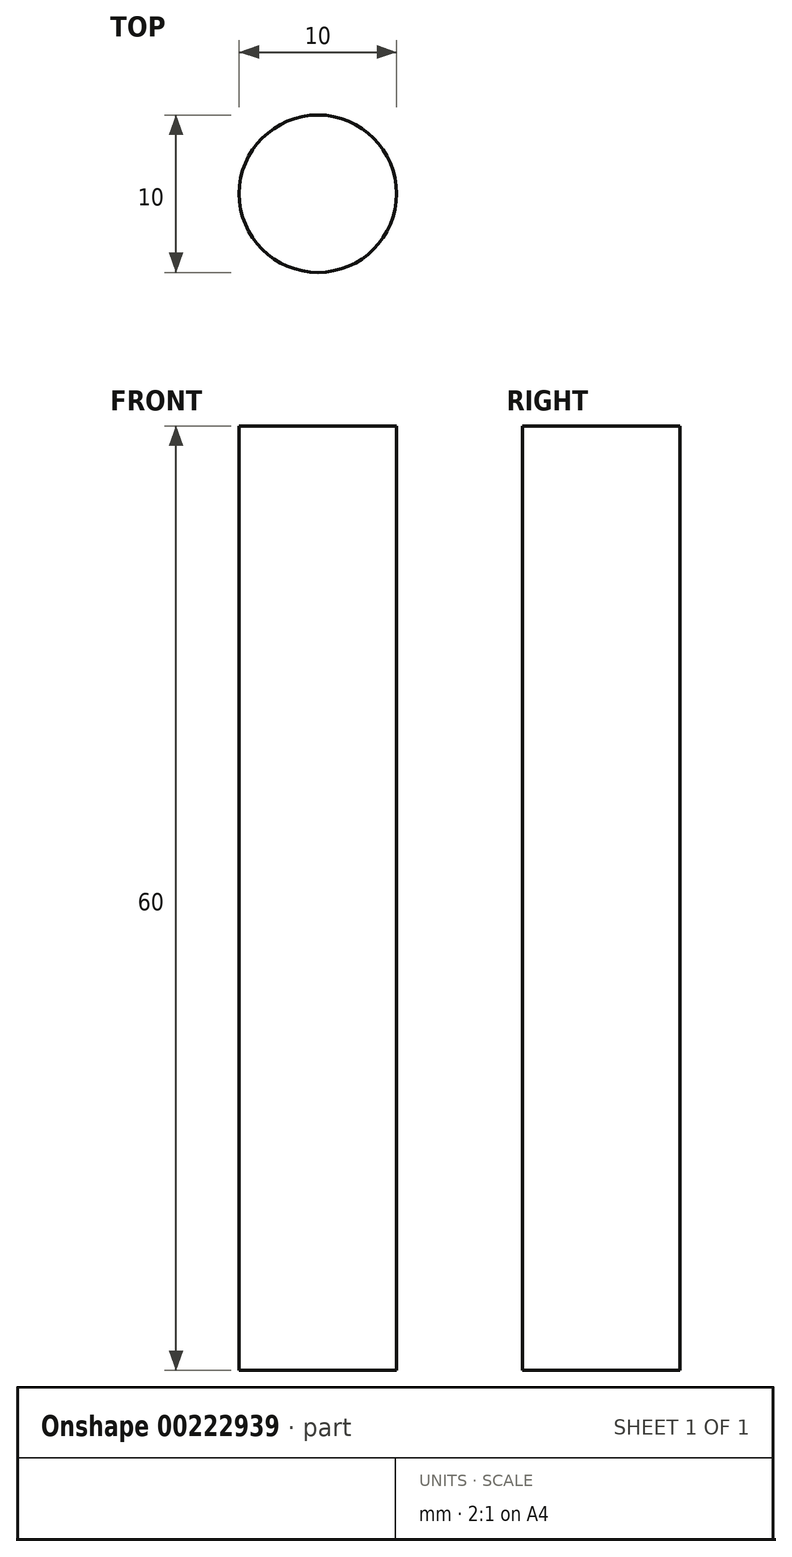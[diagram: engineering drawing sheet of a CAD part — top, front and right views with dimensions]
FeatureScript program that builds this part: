
annotation { "Feature Type Name" : "Feature", "Feature Type Description" : "" }
export const myFeature = defineFeature(function(context is Context, id is Id, definition is map)
    precondition{}
    {
        {
            var Q0;
            Q0=qCreatedBy(makeId("Top.planeOp"),FACE);
            var sketch = newSketch(context, id + "F0", { "sketchPlane" : qUnion([Q0])});
            skCircle(sketch, "E0", {"center": v(0, 0) * mm, "radius": 5 * mm});
            skSolve(sketch);
        }
        {
            var Q0;
            Q0=makeQuery(id+"F0.imprint","IMPRINT",FACE,{"disambiguationData":[TD([[makeQuery(id+"F0.imprint","IMPRINT",EDGE,{"derivedFrom":sQuery(id+"F0.wireOp",EDGE,"E0")}),1.0]])]});
            extrude(context, id + "F1", {"entities" : qUnion([Q0]), "endBound" : BoundingType.SYMMETRIC, "depth" : 60 * mm});
        }
    });
